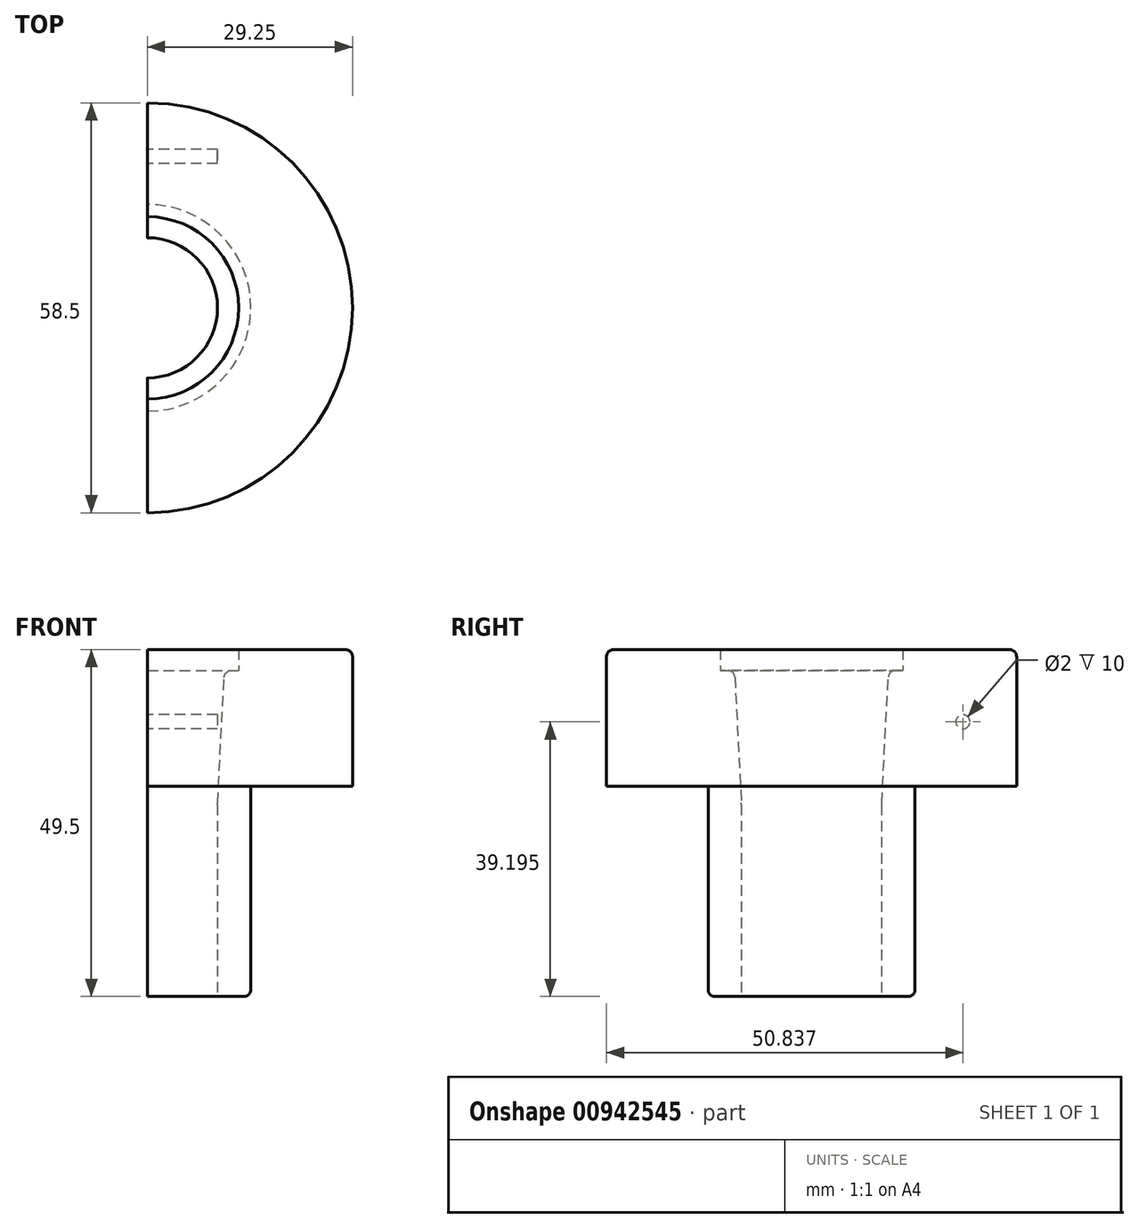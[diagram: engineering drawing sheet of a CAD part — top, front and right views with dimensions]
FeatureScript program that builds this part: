
annotation { "Feature Type Name" : "Feature", "Feature Type Description" : "" }
export const myFeature = defineFeature(function(context is Context, id is Id, definition is map)
    precondition{}
    {
        {
            var Q0;
            Q0=qCreatedBy(makeId("Top.planeOp"),FACE);
            var sketch = newSketch(context, id + "F0", { "sketchPlane" : qUnion([Q0])});
            skCircle(sketch, "E0", {"center": v(0, 0) * mm, "radius": 14.75 * mm});
            skSolve(sketch);
        }
        {
            var Q0;
            Q0 = qSketchRegion(id + "F0", true);
            extrude(context, id + "F1", {"entities" : qUnion([Q0]), "oppositeDirection" : true, "depth" : 30 * mm, "offsetDistance" : 25 * mm});
        }
        {
            var Q0;
            Q0=makeQuery(id+"F1.opExtrude","CAP_FACE",FACE,{"disambiguationData":[OSD([sQuery(id+"F0.wireOp",EDGE,"E0")])],"isStart":true});
            var sketch = newSketch(context, id + "F2", { "sketchPlane" : qUnion([Q0])});
            skCircle(sketch, "E1", {"center": v(0, 0) * mm, "radius": 29.25 * mm});
            skSolve(sketch);
        }
        {
            var Q0;
            Q0 = qSketchRegion(id + "F2", true);
            extrude(context, id + "F3", {"entities" : qUnion([Q0]), "operationType" : NewBodyOperationType.ADD, "depth" : 19.5 * mm, "offsetDistance" : 25 * mm});
        }
        {
            var Q0;
            Q0=qCreatedBy(makeId("Right.planeOp"),FACE);
            var sketch = newSketch(context, id + "F4", { "sketchPlane" : qUnion([Q0])});
            skLineSegment(sketch, "E2.0", {"start": v(-29.25, 19.5) * mm, "end": v(29.25, 19.5) * mm, "construction": true});
            skLineSegment(sketch, "E3", {"start": v(13, 19.5) * mm, "end": v(13, 16.5) * mm});
            skPoint(sketch, "E4", {"position": v(11, 16.5) * mm});
            skLineSegment(sketch, "E5", {"start": v(32.88, -2.5) * mm, "end": v(-32.2, -2.5) * mm, "construction": true});
            skPoint(sketch, "E6", {"position": v(10, -2.5) * mm});
            skLineSegment(sketch, "E7", {"start": v(13, 16.5) * mm, "end": v(11, 16.5) * mm});
            skLineSegment(sketch, "E8", {"start": v(11, 16.5) * mm, "end": v(10, -2.5) * mm});
            skLineSegment(sketch, "E9.0", {"start": v(-14.75, -30) * mm, "end": v(14.75, -30) * mm, "construction": true});
            skLineSegment(sketch, "E10", {"start": v(10, -2.5) * mm, "end": v(10, -30) * mm});
            skLineSegment(sketch, "E11", {"start": v(0, 52.22) * mm, "end": v(0, -41.8) * mm, "construction": true});
            skLineSegment(sketch, "E12", {"start": v(10, -30) * mm, "end": v(0, -30) * mm});
            skLineSegment(sketch, "E13", {"start": v(0, -30) * mm, "end": v(0, 19.5) * mm});
            skLineSegment(sketch, "E14", {"start": v(0, 19.5) * mm, "end": v(13, 19.5) * mm});
            skSolve(sketch);
        }
        {
            var Q0;
            Q0=makeQuery(id+"F4.imprint","IMPRINT",FACE,{"disambiguationData":[TD([[makeQuery(id+"F4.imprint","IMPRINT",EDGE,{"derivedFrom":sQuery(id+"F4.wireOp",EDGE,"E3")}),-1.0]])]});
            var Q1;
            Q1=sQuery(id+"F4.wireOp",EDGE,"E11");
            revolve(context, id + "F5", {"operationType" : NewBodyOperationType.REMOVE, "surfaceOperationType" : NewSurfaceOperationType.NEW, "entities" : qUnion([Q0]), "axis" : qUnion([Q1]), "revolveType" : RevolveType.FULL, "oppositeDirection" : true});
        }
        {
            var Q0;
            Q0=makeQuery(id+"F3.opExtrude","CAP_EDGE",EDGE,{"disambiguationData":[OSD([sQuery(id+"F2.wireOp",EDGE,"E1")])],"isStart":false});
            var Q1;
            Q1=makeQuery(id+"F5.boolean.opBoolean","COPY",EDGE,{"derivedFrom":makeQuery(id+"F5.opRevolve","SWEPT_EDGE",EDGE,{"disambiguationData":[OSD([sQuery(id+"F4.wireOp",EDGE,"E7"),sQuery(id+"F4.wireOp",EDGE,"E8")])]})});
            var Q2;
            Q2=makeQuery(id+"F5.boolean.opBoolean","COPY",EDGE,{"derivedFrom":makeQuery(id+"F5.opRevolve","SWEPT_EDGE",EDGE,{"disambiguationData":[OSD([sQuery(id+"F4.wireOp",EDGE,"E3"),sQuery(id+"F4.wireOp",EDGE,"E14")])]})});
            var Q3;
            Q3=makeQuery(id+"F5.boolean.opBoolean","COPY",EDGE,{"derivedFrom":makeQuery(id+"F5.opRevolve","SWEPT_EDGE",EDGE,{"disambiguationData":[OSD([sQuery(id+"F4.wireOp",EDGE,"E10"),sQuery(id+"F4.wireOp",EDGE,"E12")])]})});
            var Q4;
            Q4=makeQuery(id+"F1.opExtrude","CAP_EDGE",EDGE,{"disambiguationData":[OSD([sQuery(id+"F0.wireOp",EDGE,"E0")])],"isStart":false});
            fillet(context, id + "F6", {"entities" : qUnion([Q0, Q1, Q2, Q3, Q4]), "radius" : 1 * mm, "tangentPropagation" : true, "allowEdgeOverflow" : false});
        }
        {
            var Q0;
            Q0=qCreatedBy(makeId("Right.planeOp"),FACE);
            cPlane(context, id + "F7", {"entities" : qUnion([Q0]), "cplaneType" : CPlaneType.OFFSET, "offset" : 0 * mm, "width" : 150 * mm, "height" : 150 * mm});
        }
        {
            var Q0;
            Q0=qCreatedBy(id+"F7.planeOp",FACE);
            var sketch = newSketch(context, id + "F8", { "sketchPlane" : qUnion([Q0])});
            skLineSegment(sketch, "E15.bottom", {"start": v(36.88, -37.32) * mm, "end": v(-36.88, -37.32) * mm});
            skLineSegment(sketch, "E15.top", {"start": v(36.88, 37.32) * mm, "end": v(-36.88, 37.32) * mm});
            skLineSegment(sketch, "E15.left", {"start": v(36.88, -37.32) * mm, "end": v(36.88, 37.32) * mm});
            skLineSegment(sketch, "E15.right", {"start": v(-36.88, -37.32) * mm, "end": v(-36.88, 37.32) * mm});
            skPoint(sketch, "E15.middle", {"position": v(0, 0) * mm});
            skSolve(sketch);
        }
        {
            var Q0;
            Q0=makeQuery(id+"F8.imprint","IMPRINT",FACE,{"disambiguationData":[TD([[makeQuery(id+"F8.imprint","IMPRINT",EDGE,{"derivedFrom":sQuery(id+"F8.wireOp",EDGE,"E15.bottom")}),-1.0]])]});
            extrude(context, id + "F9", {"entities" : qUnion([Q0]), "operationType" : NewBodyOperationType.REMOVE, "endBound" : BoundingType.THROUGH_ALL, "oppositeDirection" : true, "depth" : 25 * mm, "offsetDistance" : 25 * mm});
        }
        {
            var Q0;
            Q0=makeQuery(id+"F5.boolean.opBoolean","COPY",EDGE,{"derivedFrom":makeQuery(id+"F5.opRevolve","SWEPT_EDGE",EDGE,{"disambiguationData":[OSD([sQuery(id+"F4.wireOp",EDGE,"E8"),sQuery(id+"F4.wireOp",EDGE,"E10")])]})});
            fillet(context, id + "F10", {"entities" : qUnion([Q0]), "radius" : 5 * mm, "tangentPropagation" : true, "allowEdgeOverflow" : false});
        }
        {
            var Q0;
            Q0=makeQuery(id+"F9.boolean.opBoolean","COPY",FACE,{"disambiguationData":[OD(1.0)],"derivedFrom":makeQuery(id+"F9.opExtrude","CAP_FACE",FACE,{"disambiguationData":[OSD([sQuery(id+"F8.wireOp",EDGE,"E15.bottom"),sQuery(id+"F8.wireOp",EDGE,"E15.top"),sQuery(id+"F8.wireOp",EDGE,"E15.left"),sQuery(id+"F8.wireOp",EDGE,"E15.right")])],"isStart":true})});
            var sketch = newSketch(context, id + "F11", { "sketchPlane" : qUnion([Q0])});
            skPoint(sketch, "E16.0", {"position": v(-13, 19.5) * mm});
            skPoint(sketch, "E17.0", {"position": v(-29.25, 0) * mm});
            skPoint(sketch, "E18.0", {"position": v(-29.25, 19.5) * mm});
            skPoint(sketch, "E19.0", {"position": v(-14.75, 0) * mm});
            skLineSegment(sketch, "E20", {"start": v(-29.25, 19.5) * mm, "end": v(-14.75, 0) * mm, "construction": true});
            skLineSegment(sketch, "E21", {"start": v(-13, 19.5) * mm, "end": v(-29.25, 0) * mm, "construction": true});
            skCircle(sketch, "E22", {"center": v(-21.59, 9.2) * mm, "radius": 1 * mm});
            skCircle(sketch, "E23.MirrorC", {"center": v(21.59, 9.2) * mm, "radius": 1 * mm});
            skSolve(sketch);
        }
        {
            var Q0;
            Q0=makeQuery(id+"F11.imprint","IMPRINT",FACE,{"disambiguationData":[TD([[makeQuery(id+"F11.imprint","IMPRINT",EDGE,{"derivedFrom":sQuery(id+"F11.wireOp",EDGE,"E22")}),1.0]])]});
            var Q1;
            Q1=makeQuery(id+"F11.imprint","IMPRINT",FACE,{"disambiguationData":[TD([[makeQuery(id+"F11.imprint","IMPRINT",EDGE,{"derivedFrom":sQuery(id+"F11.wireOp",EDGE,"E23.MirrorC")}),-1.0]])]});
            extrude(context, id + "F12", {"entities" : qUnion([Q0, Q1]), "operationType" : NewBodyOperationType.REMOVE, "oppositeDirection" : true, "depth" : 10 * mm, "offsetDistance" : 25 * mm});
        }
    });
